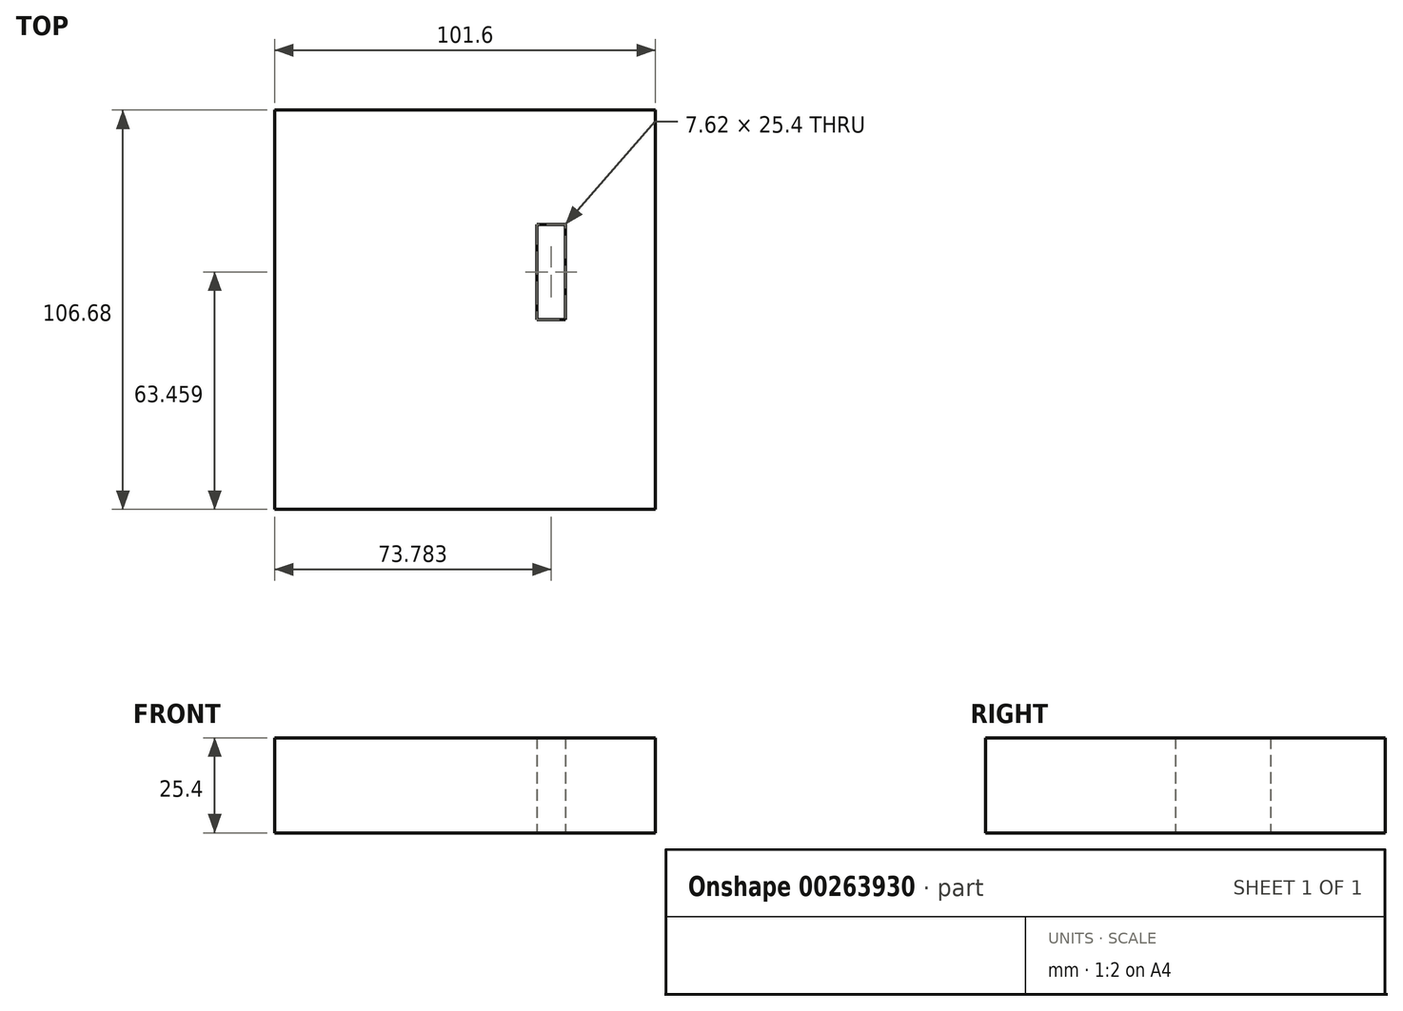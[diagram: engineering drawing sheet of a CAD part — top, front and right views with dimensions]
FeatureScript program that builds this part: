
annotation { "Feature Type Name" : "Feature", "Feature Type Description" : "" }
export const myFeature = defineFeature(function(context is Context, id is Id, definition is map)
    precondition{}
    {
        {
            var Q0;
            Q0=qCreatedBy(makeId("Top.planeOp"),FACE);
            var sketch = newSketch(context, id + "F0", { "sketchPlane" : qUnion([Q0])});
            skLineSegment(sketch, "E0.bottom", {"start": v(50.8, -53.34) * mm, "end": v(-50.8, -53.34) * mm});
            skLineSegment(sketch, "E0.top", {"start": v(50.8, 53.34) * mm, "end": v(-50.8, 53.34) * mm});
            skLineSegment(sketch, "E0.left", {"start": v(50.8, -53.34) * mm, "end": v(50.8, 53.34) * mm});
            skLineSegment(sketch, "E0.right", {"start": v(-50.8, -53.34) * mm, "end": v(-50.8, 53.34) * mm});
            skPoint(sketch, "E0.middle", {"position": v(0, 0) * mm});
            skLineSegment(sketch, "E1.bottom", {"start": v(19.17, 22.82) * mm, "end": v(26.8, 22.82) * mm});
            skLineSegment(sketch, "E1.top", {"start": v(19.17, -2.58) * mm, "end": v(26.8, -2.58) * mm});
            skLineSegment(sketch, "E1.left", {"start": v(19.17, 22.82) * mm, "end": v(19.17, -2.58) * mm});
            skLineSegment(sketch, "E1.right", {"start": v(26.8, 22.82) * mm, "end": v(26.8, -2.58) * mm});
            skSolve(sketch);
        }
        {
            var Q0;
            Q0 = qSketchRegion(id + "F0", true);
            extrude(context, id + "F1", {"entities" : qUnion([Q0]), "depth" : 25.4 * mm});
        }
    });
